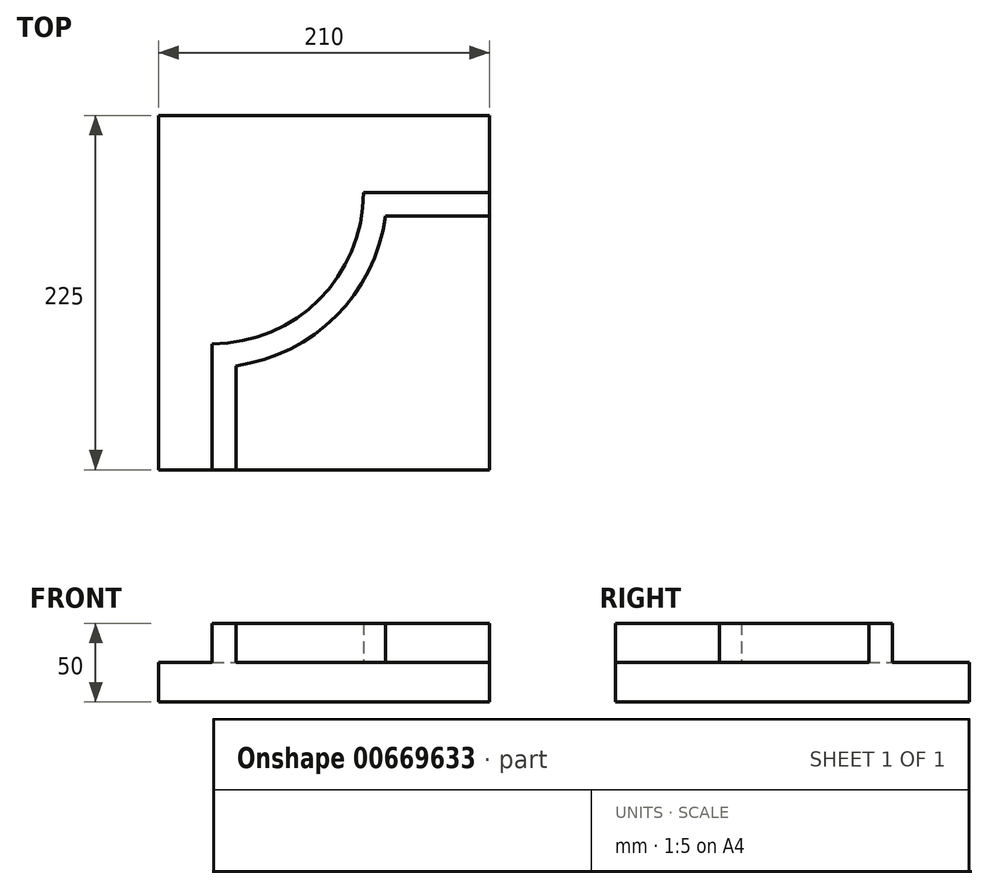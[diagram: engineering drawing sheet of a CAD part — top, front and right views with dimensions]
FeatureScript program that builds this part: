
annotation { "Feature Type Name" : "Feature", "Feature Type Description" : "" }
export const myFeature = defineFeature(function(context is Context, id is Id, definition is map)
    precondition{}
    {
        {
            var Q0;
            Q0=qCreatedBy(makeId("Top.planeOp"),FACE);
            var sketch = newSketch(context, id + "F0", { "sketchPlane" : qUnion([Q0])});
            skLineSegment(sketch, "E0.bottom", {"start": v(105, -112.5) * mm, "end": v(-105, -112.5) * mm});
            skLineSegment(sketch, "E0.top", {"start": v(105, 112.5) * mm, "end": v(-105, 112.5) * mm});
            skLineSegment(sketch, "E0.left", {"start": v(105, -112.5) * mm, "end": v(105, 112.5) * mm});
            skLineSegment(sketch, "E0.right", {"start": v(-105, -112.5) * mm, "end": v(-105, 112.5) * mm});
            skPoint(sketch, "E0.middle", {"position": v(0, 0) * mm});
            skSolve(sketch);
        }
        {
            var Q0;
            Q0=makeQuery(id+"F0.imprint","IMPRINT",FACE,{"disambiguationData":[TD([[makeQuery(id+"F0.imprint","IMPRINT",EDGE,{"derivedFrom":sQuery(id+"F0.wireOp",EDGE,"E0.bottom")}),-1.0]])]});
            extrude(context, id + "F1", {"entities" : qUnion([Q0]), "depth" : 25 * mm, "offsetDistance" : 25 * mm});
        }
        {
            var Q0;
            Q0=makeQuery(id+"F1.opExtrude","CAP_FACE",FACE,{"disambiguationData":[OSD([sQuery(id+"F0.wireOp",EDGE,"E0.bottom"),sQuery(id+"F0.wireOp",EDGE,"E0.top"),sQuery(id+"F0.wireOp",EDGE,"E0.left"),sQuery(id+"F0.wireOp",EDGE,"E0.right")])],"isStart":false});
            var sketch = newSketch(context, id + "F2", { "sketchPlane" : qUnion([Q0])});
            skLineSegment(sketch, "E1", {"start": v(-71, -112.5) * mm, "end": v(-71, -32.5) * mm});
            skLineSegment(sketch, "E2", {"start": v(105, 63.5) * mm, "end": v(25, 63.5) * mm});
            skArc(sketch, "E3", {"start": v(-71, -32.5) * mm, "mid": v(-3.12, -4.38) * mm, "end": v(25, 63.5) * mm});
            skLineSegment(sketch, "E4", {"start": v(-71, 63.5) * mm, "end": v(-71, -32.5) * mm, "construction": true});
            skLineSegment(sketch, "E5", {"start": v(-71, 63.5) * mm, "end": v(25, 63.5) * mm, "construction": true});
            skLineSegment(sketch, "E6.0", {"start": v(-56, -112.5) * mm, "end": v(-56, -46.48) * mm});
            skArc(sketch, "E6.1", {"start": v(-56, -46.48) * mm, "mid": v(7.49, -14.99) * mm, "end": v(38.98, 48.5) * mm});
            skLineSegment(sketch, "E6.2", {"start": v(105, 48.5) * mm, "end": v(38.98, 48.5) * mm});
            skSolve(sketch);
        }
        {
            var Q0;
            {var subQ4=sQuery(id+"F2.wireOp",EDGE,"E1");Q0=makeQuery(id+"F2.imprint","IMPRINT",FACE,{"disambiguationData":[TD([[makeQuery(id+"F2.imprint","IMPRINT",EDGE,{"derivedFrom":subQ4}),-1.0]])]});}
            extrude(context, id + "F3", {"entities" : qUnion([Q0]), "operationType" : NewBodyOperationType.ADD, "depth" : 25 * mm, "offsetDistance" : 25 * mm});
        }
    });
